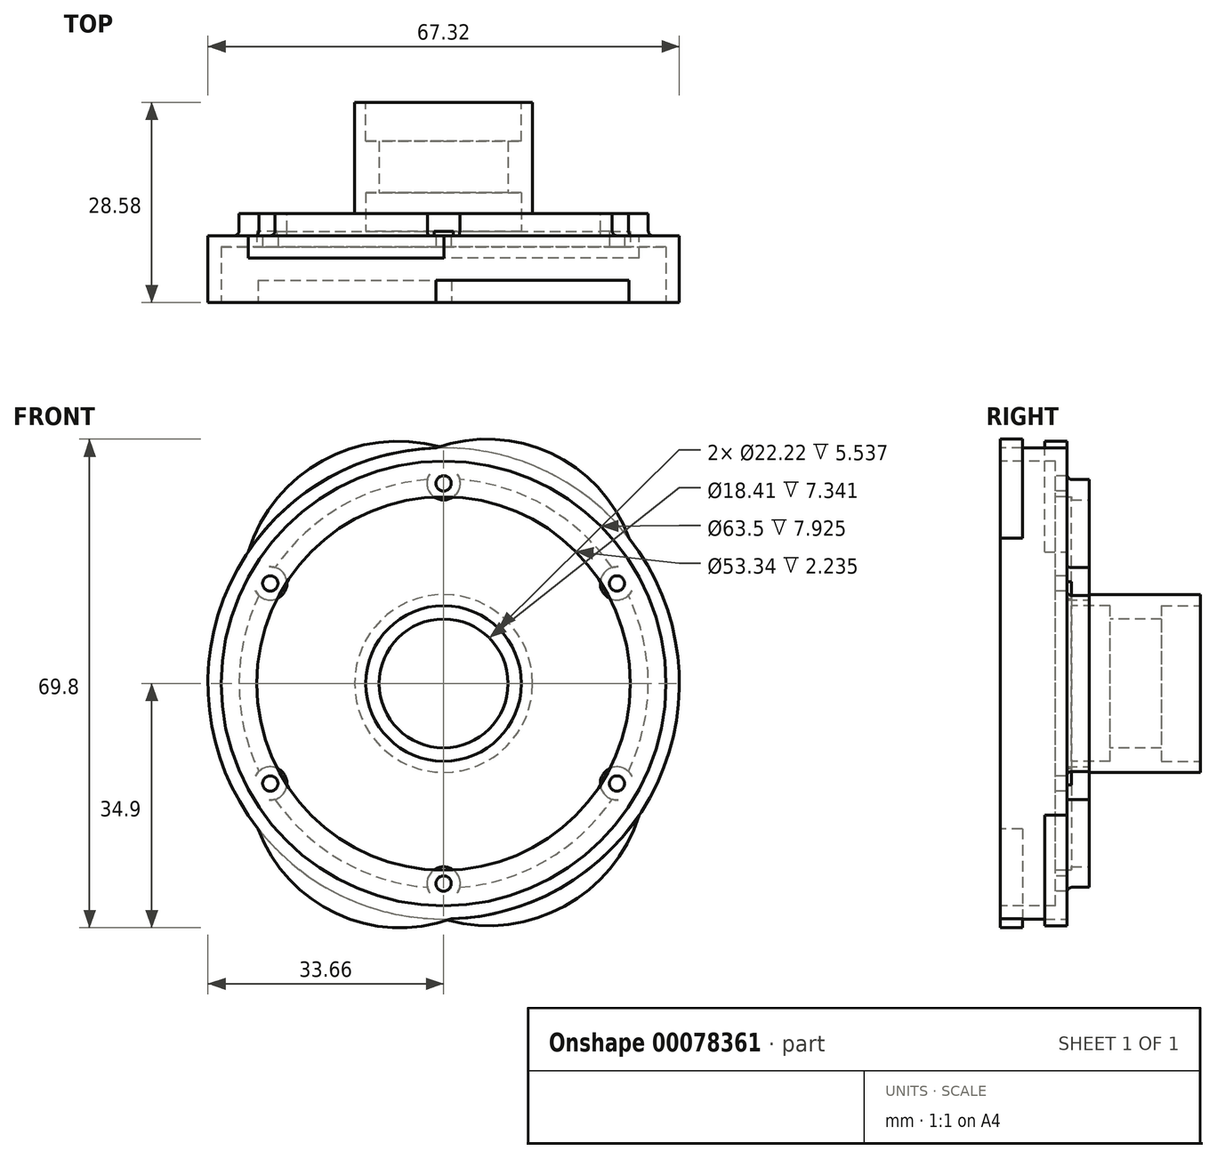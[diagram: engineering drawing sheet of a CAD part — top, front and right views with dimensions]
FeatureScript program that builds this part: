
annotation { "Feature Type Name" : "Feature", "Feature Type Description" : "" }
export const myFeature = defineFeature(function(context is Context, id is Id, definition is map)
    precondition{}
    {
        {
            var Q0;
            Q0=qCreatedBy(makeId("Front.planeOp"),FACE);
            var sketch = newSketch(context, id + "F0", { "sketchPlane" : qUnion([Q0])});
            skCircle(sketch, "E0", {"center": v(0, 0) * mm, "radius": 33.66 * mm});
            skSolve(sketch);
        }
        {
            var Q0;
            Q0 = qSketchRegion(id + "F0", true);
            extrude(context, id + "F1", {"entities" : qUnion([Q0]), "depth" : 28.57 * mm});
        }
        {
            var Q0;
            Q0=makeQuery(id+"F1.opExtrude","CAP_FACE",FACE,{"disambiguationData":[OSD([sQuery(id+"F0.wireOp",EDGE,"E0")])],"isStart":true});
            var sketch = newSketch(context, id + "F2", { "sketchPlane" : qUnion([Q0])});
            skCircle(sketch, "E1", {"center": v(0, 0) * mm, "radius": 12.7 * mm});
            skCircle(sketch, "E2", {"center": v(0, 0) * mm, "radius": 43.85 * mm});
            skSolve(sketch);
        }
        {
            var Q0;
            Q0 = qSketchRegion(id + "F2", true);
            extrude(context, id + "F3", {"entities" : qUnion([Q0]), "operationType" : NewBodyOperationType.REMOVE, "oppositeDirection" : true, "depth" : 15.88 * mm});
        }
        {
            var Q0;
            Q0=makeQuery(id+"F1.opExtrude","CAP_FACE",FACE,{"disambiguationData":[OSD([sQuery(id+"F0.wireOp",EDGE,"E0")])],"isStart":false});
            var sketch = newSketch(context, id + "F4", { "sketchPlane" : qUnion([Q0])});
            skCircle(sketch, "E3", {"center": v(0, 0) * mm, "radius": 31.75 * mm});
            skSolve(sketch);
        }
        {
            var Q0;
            Q0 = qSketchRegion(id + "F4", true);
            extrude(context, id + "F5", {"entities" : qUnion([Q0]), "operationType" : NewBodyOperationType.REMOVE, "oppositeDirection" : true, "depth" : 7.92 * mm});
        }
        {
            var Q0;
            Q0=makeQuery(id+"F5.boolean.opBoolean","COPY",FACE,{"derivedFrom":makeQuery(id+"F5.opExtrude","CAP_FACE",FACE,{"disambiguationData":[OSD([sQuery(id+"F4.wireOp",EDGE,"E3")])],"isStart":false})});
            var sketch = newSketch(context, id + "F6", { "sketchPlane" : qUnion([Q0])});
            skCircle(sketch, "E4", {"center": v(0, 0) * mm, "radius": 26.67 * mm});
            skSolve(sketch);
        }
        {
            var Q0;
            Q0 = qSketchRegion(id + "F6", true);
            extrude(context, id + "F7", {"entities" : qUnion([Q0]), "operationType" : NewBodyOperationType.REMOVE, "oppositeDirection" : true, "depth" : 2.24 * mm});
        }
        {
            var Q0;
            Q0=makeQuery(id+"F7.boolean.opBoolean","COPY",FACE,{"derivedFrom":makeQuery(id+"F7.opExtrude","CAP_FACE",FACE,{"disambiguationData":[OSD([sQuery(id+"F6.wireOp",EDGE,"E4")])],"isStart":false})});
            var sketch = newSketch(context, id + "F8", { "sketchPlane" : qUnion([Q0])});
            skCircle(sketch, "E5", {"center": v(0, 0) * mm, "radius": 11.1 * mm});
            skSolve(sketch);
        }
        {
            var Q0;
            Q0 = qSketchRegion(id + "F8", true);
            extrude(context, id + "F9", {"entities" : qUnion([Q0]), "operationType" : NewBodyOperationType.REMOVE, "oppositeDirection" : true, "depth" : 5.54 * mm});
        }
        {
            var Q0;
            Q0=makeQuery(id+"F9.boolean.opBoolean","COPY",FACE,{"derivedFrom":makeQuery(id+"F9.opExtrude","CAP_FACE",FACE,{"disambiguationData":[OSD([sQuery(id+"F8.wireOp",EDGE,"E5")])],"isStart":false})});
            var sketch = newSketch(context, id + "F10", { "sketchPlane" : qUnion([Q0])});
            skCircle(sketch, "E6", {"center": v(0, 0) * mm, "radius": 9.2 * mm});
            skSolve(sketch);
        }
        {
            var Q0;
            Q0=makeQuery(id+"F10.imprint","IMPRINT",FACE,{"disambiguationData":[TD([[makeQuery(id+"F10.imprint","IMPRINT",EDGE,{"derivedFrom":sQuery(id+"F10.wireOp",EDGE,"E6")}),1.0]])]});
            extrude(context, id + "F11", {"entities" : qUnion([Q0]), "operationType" : NewBodyOperationType.REMOVE, "oppositeDirection" : true, "depth" : 25.4 * mm});
        }
        {
            var Q0;
            Q0=makeQuery(id+"F1.opExtrude","CAP_FACE",FACE,{"disambiguationData":[OSD([sQuery(id+"F0.wireOp",EDGE,"E0")])],"isStart":true});
            var sketch = newSketch(context, id + "F12", { "sketchPlane" : qUnion([Q0])});
            skCircle(sketch, "E7", {"center": v(0, 0) * mm, "radius": 11.1 * mm});
            skSolve(sketch);
        }
        {
            var Q0;
            Q0 = qSketchRegion(id + "F12", true);
            extrude(context, id + "F13", {"entities" : qUnion([Q0]), "operationType" : NewBodyOperationType.REMOVE, "oppositeDirection" : true, "depth" : 5.54 * mm});
        }
        {
            var Q0;
            Q0=makeQuery(id+"F3.boolean.opBoolean","COPY",FACE,{"derivedFrom":makeQuery(id+"F3.opExtrude","CAP_FACE",FACE,{"disambiguationData":[OSD([sQuery(id+"F2.wireOp",EDGE,"E1"),sQuery(id+"F2.wireOp",EDGE,"E2")])],"isStart":false})});
            var sketch = newSketch(context, id + "F14", { "sketchPlane" : qUnion([Q0])});
            skCircle(sketch, "E8", {"center": v(0, 0) * mm, "radius": 29.2 * mm});
            skCircle(sketch, "E9", {"center": v(0, 0) * mm, "radius": 43.76 * mm});
            skSolve(sketch);
        }
        {
            var Q0;
            Q0 = qSketchRegion(id + "F14", true);
            extrude(context, id + "F15", {"entities" : qUnion([Q0]), "operationType" : NewBodyOperationType.REMOVE, "oppositeDirection" : true, "depth" : 3.17 * mm});
        }
        {
            var Q0;
            Q0=makeQuery(id+"F5.boolean.opBoolean","COPY",FACE,{"derivedFrom":makeQuery(id+"F5.opExtrude","CAP_FACE",FACE,{"disambiguationData":[OSD([sQuery(id+"F4.wireOp",EDGE,"E3")])],"isStart":false})});
            var sketch = newSketch(context, id + "F16", { "sketchPlane" : qUnion([Q0])});
            skCircle(sketch, "E10", {"center": v(0, 28.58) * mm, "radius": 1.1 * mm});
            skCircle(sketch, "E11.1.0", {"center": v(-24.75, 14.29) * mm, "radius": 1.1 * mm});
            skCircle(sketch, "E11.2.0", {"center": v(-24.75, -14.29) * mm, "radius": 1.1 * mm});
            skCircle(sketch, "E11.3.0", {"center": v(0, -28.58) * mm, "radius": 1.1 * mm});
            skCircle(sketch, "E11.4.0", {"center": v(24.75, -14.29) * mm, "radius": 1.1 * mm});
            skCircle(sketch, "E11.5.0", {"center": v(24.75, 14.29) * mm, "radius": 1.1 * mm});
            skPoint(sketch, "E11.center", {"position": v(0, 0) * mm});
            skSolve(sketch);
        }
        {
            var Q0;
            Q0 = qSketchRegion(id + "F16", true);
            extrude(context, id + "F17", {"entities" : qUnion([Q0]), "operationType" : NewBodyOperationType.REMOVE, "oppositeDirection" : true, "depth" : 25.4 * mm});
        }
        {
            var Q0;
            Q0=makeQuery(id+"F3.boolean.opBoolean","COPY",FACE,{"derivedFrom":makeQuery(id+"F3.opExtrude","CAP_FACE",FACE,{"disambiguationData":[OSD([sQuery(id+"F2.wireOp",EDGE,"E1"),sQuery(id+"F2.wireOp",EDGE,"E2")])],"isStart":false})});
            var sketch = newSketch(context, id + "F18", { "sketchPlane" : qUnion([Q0])});
            skCircle(sketch, "E12", {"center": v(0, 28.58) * mm, "radius": 2.37 * mm});
            skCircle(sketch, "E13.1.0", {"center": v(-24.75, 14.29) * mm, "radius": 2.37 * mm});
            skCircle(sketch, "E13.2.0", {"center": v(-24.75, -14.29) * mm, "radius": 2.37 * mm});
            skCircle(sketch, "E13.3.0", {"center": v(0, -28.58) * mm, "radius": 2.37 * mm});
            skCircle(sketch, "E13.4.0", {"center": v(24.75, -14.29) * mm, "radius": 2.37 * mm});
            skCircle(sketch, "E13.5.0", {"center": v(24.75, 14.29) * mm, "radius": 2.37 * mm});
            skPoint(sketch, "E13.center", {"position": v(0, 0) * mm});
            skSolve(sketch);
        }
        {
            var Q0;
            Q0 = qSketchRegion(id + "F18", true);
            extrude(context, id + "F19", {"entities" : qUnion([Q0]), "operationType" : NewBodyOperationType.REMOVE, "oppositeDirection" : true, "depth" : 3.17 * mm});
        }
        {
            var Q0;
            {var subQ0=sQuery(id+"F14.wireOp",EDGE,"E8");Q0=makeQuery(id+"F17.boolean.opBoolean","SPLIT",EDGE,{"disambiguationData":[TD([makeQuery(id+"F15.boolean.opBoolean","COPY",FACE,{"derivedFrom":makeQuery(id+"F15.opExtrude","SWEPT_FACE",FACE,{"disambiguationData":[OSD([subQ0])]})}),makeQuery(id+"F15.boolean.opBoolean","COPY",FACE,{"derivedFrom":makeQuery(id+"F15.opExtrude","CAP_FACE",FACE,{"disambiguationData":[OSD([subQ0,sQuery(id+"F14.wireOp",EDGE,"E9")])],"isStart":false})}),makeQuery(id+"F17.opExtrude","SWEPT_FACE",FACE,{"disambiguationData":[OSD([sQuery(id+"F16.wireOp",EDGE,"E10")])]}),makeQuery(id+"F17.opExtrude","SWEPT_FACE",FACE,{"disambiguationData":[OSD([sQuery(id+"F16.wireOp",EDGE,"E11.5.0")])]})])],"derivedFrom":makeQuery(id+"F15.boolean.opBoolean","COPY",EDGE,{"derivedFrom":makeQuery(id+"F15.opExtrude","CAP_EDGE",EDGE,{"disambiguationData":[OSD([subQ0])],"isStart":false})})});}
            var Q1;
            {var subQ0=sQuery(id+"F14.wireOp",EDGE,"E8");Q1=makeQuery(id+"F17.boolean.opBoolean","SPLIT",EDGE,{"disambiguationData":[TD([makeQuery(id+"F15.boolean.opBoolean","COPY",FACE,{"derivedFrom":makeQuery(id+"F15.opExtrude","SWEPT_FACE",FACE,{"disambiguationData":[OSD([subQ0])]})}),makeQuery(id+"F15.boolean.opBoolean","COPY",FACE,{"derivedFrom":makeQuery(id+"F15.opExtrude","CAP_FACE",FACE,{"disambiguationData":[OSD([subQ0,sQuery(id+"F14.wireOp",EDGE,"E9")])],"isStart":false})}),makeQuery(id+"F17.opExtrude","SWEPT_FACE",FACE,{"disambiguationData":[OSD([sQuery(id+"F16.wireOp",EDGE,"E11.4.0")])]}),makeQuery(id+"F17.opExtrude","SWEPT_FACE",FACE,{"disambiguationData":[OSD([sQuery(id+"F16.wireOp",EDGE,"E11.5.0")])]})])],"derivedFrom":makeQuery(id+"F15.boolean.opBoolean","COPY",EDGE,{"derivedFrom":makeQuery(id+"F15.opExtrude","CAP_EDGE",EDGE,{"disambiguationData":[OSD([subQ0])],"isStart":false})})});}
            var Q2;
            {var subQ0=sQuery(id+"F14.wireOp",EDGE,"E8");Q2=makeQuery(id+"F17.boolean.opBoolean","SPLIT",EDGE,{"disambiguationData":[TD([makeQuery(id+"F15.boolean.opBoolean","COPY",FACE,{"derivedFrom":makeQuery(id+"F15.opExtrude","SWEPT_FACE",FACE,{"disambiguationData":[OSD([subQ0])]})}),makeQuery(id+"F15.boolean.opBoolean","COPY",FACE,{"derivedFrom":makeQuery(id+"F15.opExtrude","CAP_FACE",FACE,{"disambiguationData":[OSD([subQ0,sQuery(id+"F14.wireOp",EDGE,"E9")])],"isStart":false})}),makeQuery(id+"F17.opExtrude","SWEPT_FACE",FACE,{"disambiguationData":[OSD([sQuery(id+"F16.wireOp",EDGE,"E11.3.0")])]}),makeQuery(id+"F17.opExtrude","SWEPT_FACE",FACE,{"disambiguationData":[OSD([sQuery(id+"F16.wireOp",EDGE,"E11.4.0")])]})])],"derivedFrom":makeQuery(id+"F15.boolean.opBoolean","COPY",EDGE,{"derivedFrom":makeQuery(id+"F15.opExtrude","CAP_EDGE",EDGE,{"disambiguationData":[OSD([subQ0])],"isStart":false})})});}
            var Q3;
            {var subQ0=sQuery(id+"F14.wireOp",EDGE,"E8");Q3=makeQuery(id+"F17.boolean.opBoolean","SPLIT",EDGE,{"disambiguationData":[TD([makeQuery(id+"F15.boolean.opBoolean","COPY",FACE,{"derivedFrom":makeQuery(id+"F15.opExtrude","SWEPT_FACE",FACE,{"disambiguationData":[OSD([subQ0])]})}),makeQuery(id+"F15.boolean.opBoolean","COPY",FACE,{"derivedFrom":makeQuery(id+"F15.opExtrude","CAP_FACE",FACE,{"disambiguationData":[OSD([subQ0,sQuery(id+"F14.wireOp",EDGE,"E9")])],"isStart":false})}),makeQuery(id+"F17.opExtrude","SWEPT_FACE",FACE,{"disambiguationData":[OSD([sQuery(id+"F16.wireOp",EDGE,"E11.1.0")])]}),makeQuery(id+"F17.opExtrude","SWEPT_FACE",FACE,{"disambiguationData":[OSD([sQuery(id+"F16.wireOp",EDGE,"E11.2.0")])]})])],"derivedFrom":makeQuery(id+"F15.boolean.opBoolean","COPY",EDGE,{"derivedFrom":makeQuery(id+"F15.opExtrude","CAP_EDGE",EDGE,{"disambiguationData":[OSD([subQ0])],"isStart":false})})});}
            var Q4;
            {var subQ0=sQuery(id+"F14.wireOp",EDGE,"E8");Q4=makeQuery(id+"F17.boolean.opBoolean","SPLIT",EDGE,{"disambiguationData":[TD([makeQuery(id+"F15.boolean.opBoolean","COPY",FACE,{"derivedFrom":makeQuery(id+"F15.opExtrude","SWEPT_FACE",FACE,{"disambiguationData":[OSD([subQ0])]})}),makeQuery(id+"F15.boolean.opBoolean","COPY",FACE,{"derivedFrom":makeQuery(id+"F15.opExtrude","CAP_FACE",FACE,{"disambiguationData":[OSD([subQ0,sQuery(id+"F14.wireOp",EDGE,"E9")])],"isStart":false})}),makeQuery(id+"F17.opExtrude","SWEPT_FACE",FACE,{"disambiguationData":[OSD([sQuery(id+"F16.wireOp",EDGE,"E10")])]}),makeQuery(id+"F17.opExtrude","SWEPT_FACE",FACE,{"disambiguationData":[OSD([sQuery(id+"F16.wireOp",EDGE,"E11.1.0")])]})])],"derivedFrom":makeQuery(id+"F15.boolean.opBoolean","COPY",EDGE,{"derivedFrom":makeQuery(id+"F15.opExtrude","CAP_EDGE",EDGE,{"disambiguationData":[OSD([subQ0])],"isStart":false})})});}
            var Q5;
            {var subQ0=sQuery(id+"F14.wireOp",EDGE,"E8");Q5=makeQuery(id+"F17.boolean.opBoolean","SPLIT",EDGE,{"disambiguationData":[TD([makeQuery(id+"F15.boolean.opBoolean","COPY",FACE,{"derivedFrom":makeQuery(id+"F15.opExtrude","SWEPT_FACE",FACE,{"disambiguationData":[OSD([subQ0])]})}),makeQuery(id+"F15.boolean.opBoolean","COPY",FACE,{"derivedFrom":makeQuery(id+"F15.opExtrude","CAP_FACE",FACE,{"disambiguationData":[OSD([subQ0,sQuery(id+"F14.wireOp",EDGE,"E9")])],"isStart":false})}),makeQuery(id+"F17.opExtrude","SWEPT_FACE",FACE,{"disambiguationData":[OSD([sQuery(id+"F16.wireOp",EDGE,"E11.2.0")])]}),makeQuery(id+"F17.opExtrude","SWEPT_FACE",FACE,{"disambiguationData":[OSD([sQuery(id+"F16.wireOp",EDGE,"E11.3.0")])]})])],"derivedFrom":makeQuery(id+"F15.boolean.opBoolean","COPY",EDGE,{"derivedFrom":makeQuery(id+"F15.opExtrude","CAP_EDGE",EDGE,{"disambiguationData":[OSD([subQ0])],"isStart":false})})});}
            var Q6;
            {var subQ0=sQuery(id+"F14.wireOp",EDGE,"E8");Q6=makeQuery(id+"F17.boolean.opBoolean","SPLIT",EDGE,{"disambiguationData":[TD([makeQuery(id+"F3.boolean.opBoolean","COPY",FACE,{"derivedFrom":makeQuery(id+"F3.opExtrude","CAP_FACE",FACE,{"disambiguationData":[OSD([sQuery(id+"F2.wireOp",EDGE,"E1"),sQuery(id+"F2.wireOp",EDGE,"E2")])],"isStart":false})}),makeQuery(id+"F15.boolean.opBoolean","COPY",FACE,{"derivedFrom":makeQuery(id+"F15.opExtrude","SWEPT_FACE",FACE,{"disambiguationData":[OSD([subQ0])]})}),makeQuery(id+"F17.opExtrude","SWEPT_FACE",FACE,{"disambiguationData":[OSD([sQuery(id+"F16.wireOp",EDGE,"E11.2.0")])]}),makeQuery(id+"F17.opExtrude","SWEPT_FACE",FACE,{"disambiguationData":[OSD([sQuery(id+"F16.wireOp",EDGE,"E11.3.0")])]})])],"derivedFrom":makeQuery(id+"F15.boolean.opBoolean","COPY",EDGE,{"derivedFrom":makeQuery(id+"F15.opExtrude","CAP_EDGE",EDGE,{"disambiguationData":[OSD([subQ0])],"isStart":true})})});}
            var Q7;
            {var subQ0=sQuery(id+"F14.wireOp",EDGE,"E8");Q7=makeQuery(id+"F17.boolean.opBoolean","SPLIT",EDGE,{"disambiguationData":[TD([makeQuery(id+"F3.boolean.opBoolean","COPY",FACE,{"derivedFrom":makeQuery(id+"F3.opExtrude","CAP_FACE",FACE,{"disambiguationData":[OSD([sQuery(id+"F2.wireOp",EDGE,"E1"),sQuery(id+"F2.wireOp",EDGE,"E2")])],"isStart":false})}),makeQuery(id+"F15.boolean.opBoolean","COPY",FACE,{"derivedFrom":makeQuery(id+"F15.opExtrude","SWEPT_FACE",FACE,{"disambiguationData":[OSD([subQ0])]})}),makeQuery(id+"F17.opExtrude","SWEPT_FACE",FACE,{"disambiguationData":[OSD([sQuery(id+"F16.wireOp",EDGE,"E11.1.0")])]}),makeQuery(id+"F17.opExtrude","SWEPT_FACE",FACE,{"disambiguationData":[OSD([sQuery(id+"F16.wireOp",EDGE,"E11.2.0")])]})])],"derivedFrom":makeQuery(id+"F15.boolean.opBoolean","COPY",EDGE,{"derivedFrom":makeQuery(id+"F15.opExtrude","CAP_EDGE",EDGE,{"disambiguationData":[OSD([subQ0])],"isStart":true})})});}
            var Q8;
            {var subQ0=sQuery(id+"F14.wireOp",EDGE,"E8");Q8=makeQuery(id+"F17.boolean.opBoolean","SPLIT",EDGE,{"disambiguationData":[TD([makeQuery(id+"F3.boolean.opBoolean","COPY",FACE,{"derivedFrom":makeQuery(id+"F3.opExtrude","CAP_FACE",FACE,{"disambiguationData":[OSD([sQuery(id+"F2.wireOp",EDGE,"E1"),sQuery(id+"F2.wireOp",EDGE,"E2")])],"isStart":false})}),makeQuery(id+"F15.boolean.opBoolean","COPY",FACE,{"derivedFrom":makeQuery(id+"F15.opExtrude","SWEPT_FACE",FACE,{"disambiguationData":[OSD([subQ0])]})}),makeQuery(id+"F17.opExtrude","SWEPT_FACE",FACE,{"disambiguationData":[OSD([sQuery(id+"F16.wireOp",EDGE,"E11.3.0")])]}),makeQuery(id+"F17.opExtrude","SWEPT_FACE",FACE,{"disambiguationData":[OSD([sQuery(id+"F16.wireOp",EDGE,"E11.4.0")])]})])],"derivedFrom":makeQuery(id+"F15.boolean.opBoolean","COPY",EDGE,{"derivedFrom":makeQuery(id+"F15.opExtrude","CAP_EDGE",EDGE,{"disambiguationData":[OSD([subQ0])],"isStart":true})})});}
            var Q9;
            {var subQ0=sQuery(id+"F14.wireOp",EDGE,"E8");Q9=makeQuery(id+"F17.boolean.opBoolean","SPLIT",EDGE,{"disambiguationData":[TD([makeQuery(id+"F3.boolean.opBoolean","COPY",FACE,{"derivedFrom":makeQuery(id+"F3.opExtrude","CAP_FACE",FACE,{"disambiguationData":[OSD([sQuery(id+"F2.wireOp",EDGE,"E1"),sQuery(id+"F2.wireOp",EDGE,"E2")])],"isStart":false})}),makeQuery(id+"F15.boolean.opBoolean","COPY",FACE,{"derivedFrom":makeQuery(id+"F15.opExtrude","SWEPT_FACE",FACE,{"disambiguationData":[OSD([subQ0])]})}),makeQuery(id+"F17.opExtrude","SWEPT_FACE",FACE,{"disambiguationData":[OSD([sQuery(id+"F16.wireOp",EDGE,"E11.4.0")])]}),makeQuery(id+"F17.opExtrude","SWEPT_FACE",FACE,{"disambiguationData":[OSD([sQuery(id+"F16.wireOp",EDGE,"E11.5.0")])]})])],"derivedFrom":makeQuery(id+"F15.boolean.opBoolean","COPY",EDGE,{"derivedFrom":makeQuery(id+"F15.opExtrude","CAP_EDGE",EDGE,{"disambiguationData":[OSD([subQ0])],"isStart":true})})});}
            var Q10;
            {var subQ0=sQuery(id+"F14.wireOp",EDGE,"E8");Q10=makeQuery(id+"F17.boolean.opBoolean","SPLIT",EDGE,{"disambiguationData":[TD([makeQuery(id+"F3.boolean.opBoolean","COPY",FACE,{"derivedFrom":makeQuery(id+"F3.opExtrude","CAP_FACE",FACE,{"disambiguationData":[OSD([sQuery(id+"F2.wireOp",EDGE,"E1"),sQuery(id+"F2.wireOp",EDGE,"E2")])],"isStart":false})}),makeQuery(id+"F15.boolean.opBoolean","COPY",FACE,{"derivedFrom":makeQuery(id+"F15.opExtrude","SWEPT_FACE",FACE,{"disambiguationData":[OSD([subQ0])]})}),makeQuery(id+"F17.opExtrude","SWEPT_FACE",FACE,{"disambiguationData":[OSD([sQuery(id+"F16.wireOp",EDGE,"E10")])]}),makeQuery(id+"F17.opExtrude","SWEPT_FACE",FACE,{"disambiguationData":[OSD([sQuery(id+"F16.wireOp",EDGE,"E11.5.0")])]})])],"derivedFrom":makeQuery(id+"F15.boolean.opBoolean","COPY",EDGE,{"derivedFrom":makeQuery(id+"F15.opExtrude","CAP_EDGE",EDGE,{"disambiguationData":[OSD([subQ0])],"isStart":true})})});}
            var Q11;
            {var subQ0=sQuery(id+"F14.wireOp",EDGE,"E8");Q11=makeQuery(id+"F17.boolean.opBoolean","SPLIT",EDGE,{"disambiguationData":[TD([makeQuery(id+"F3.boolean.opBoolean","COPY",FACE,{"derivedFrom":makeQuery(id+"F3.opExtrude","CAP_FACE",FACE,{"disambiguationData":[OSD([sQuery(id+"F2.wireOp",EDGE,"E1"),sQuery(id+"F2.wireOp",EDGE,"E2")])],"isStart":false})}),makeQuery(id+"F15.boolean.opBoolean","COPY",FACE,{"derivedFrom":makeQuery(id+"F15.opExtrude","SWEPT_FACE",FACE,{"disambiguationData":[OSD([subQ0])]})}),makeQuery(id+"F17.opExtrude","SWEPT_FACE",FACE,{"disambiguationData":[OSD([sQuery(id+"F16.wireOp",EDGE,"E10")])]}),makeQuery(id+"F17.opExtrude","SWEPT_FACE",FACE,{"disambiguationData":[OSD([sQuery(id+"F16.wireOp",EDGE,"E11.1.0")])]})])],"derivedFrom":makeQuery(id+"F15.boolean.opBoolean","COPY",EDGE,{"derivedFrom":makeQuery(id+"F15.opExtrude","CAP_EDGE",EDGE,{"disambiguationData":[OSD([subQ0])],"isStart":true})})});}
            fillet(context, id + "F20", {"entities" : qUnion([Q0, Q1, Q2, Q3, Q4, Q5, Q6, Q7, Q8, Q9, Q10, Q11]), "radius" : 0.76 * mm, "tangentPropagation" : true, "allowEdgeOverflow" : false});
        }
        {
            var Q0;
            Q0=makeQuery(id+"F1.opExtrude","CAP_FACE",FACE,{"disambiguationData":[OSD([sQuery(id+"F0.wireOp",EDGE,"E0")])],"isStart":false});
            var sketch = newSketch(context, id + "F21", { "sketchPlane" : qUnion([Q0])});
            skLineSegment(sketch, "E14", {"start": v(0, 0) * mm, "end": v(17.9, 38.37) * mm, "construction": true});
            skArc(sketch, "E15", {"start": v(27.29, 18.08) * mm, "mid": v(15.33, 32.87) * mm, "end": v(-3.69, 32.53) * mm});
            skArc(sketch, "E16", {"start": v(27.29, 18.08) * mm, "mid": v(13.83, 29.67) * mm, "end": v(-3.69, 32.53) * mm});
            skArc(sketch, "E17.MirrorCS", {"start": v(3.69, -32.53) * mm, "mid": v(-13.83, -29.67) * mm, "end": v(-27.29, -18.08) * mm});
            skArc(sketch, "E18.MirrorCS", {"start": v(3.69, -32.53) * mm, "mid": v(-15.33, -32.87) * mm, "end": v(-27.29, -18.08) * mm});
            skSolve(sketch);
        }
        {
            var Q0;
            Q0 = qSketchRegion(id + "F21", true);
            extrude(context, id + "F22", {"entities" : qUnion([Q0]), "operationType" : NewBodyOperationType.ADD, "oppositeDirection" : true, "depth" : 3.17 * mm});
        }
        {
            var Q0;
            Q0=makeQuery(id+"F19.boolean.opBoolean","MERGE",FACE,{"derivedFrom":[makeQuery(id+"F15.boolean.opBoolean","COPY",FACE,{"derivedFrom":makeQuery(id+"F15.opExtrude","CAP_FACE",FACE,{"disambiguationData":[OSD([sQuery(id+"F14.wireOp",EDGE,"E8"),sQuery(id+"F14.wireOp",EDGE,"E9")])],"isStart":false})}),makeQuery(id+"F19.opExtrude","CAP_FACE",FACE,{"disambiguationData":[OSD([sQuery(id+"F18.wireOp",EDGE,"E12")])],"isStart":false}),makeQuery(id+"F19.opExtrude","CAP_FACE",FACE,{"disambiguationData":[OSD([sQuery(id+"F18.wireOp",EDGE,"E13.1.0")])],"isStart":false}),makeQuery(id+"F19.opExtrude","CAP_FACE",FACE,{"disambiguationData":[OSD([sQuery(id+"F18.wireOp",EDGE,"E13.2.0")])],"isStart":false}),makeQuery(id+"F19.opExtrude","CAP_FACE",FACE,{"disambiguationData":[OSD([sQuery(id+"F18.wireOp",EDGE,"E13.3.0")])],"isStart":false}),makeQuery(id+"F19.opExtrude","CAP_FACE",FACE,{"disambiguationData":[OSD([sQuery(id+"F18.wireOp",EDGE,"E13.4.0")])],"isStart":false}),makeQuery(id+"F19.opExtrude","CAP_FACE",FACE,{"disambiguationData":[OSD([sQuery(id+"F18.wireOp",EDGE,"E13.5.0")])],"isStart":false})]});
            var sketch = newSketch(context, id + "F23", { "sketchPlane" : qUnion([Q0])});
            skLineSegment(sketch, "E19", {"start": v(0, 0) * mm, "end": v(20.67, 38.87) * mm, "construction": true});
            skArc(sketch, "E20", {"start": v(28.64, 15.79) * mm, "mid": v(17, 31.97) * mm, "end": v(-2.93, 32.57) * mm});
            skArc(sketch, "E21", {"start": v(28.64, 15.79) * mm, "mid": v(15.35, 28.87) * mm, "end": v(-2.93, 32.57) * mm});
            skArc(sketch, "E22.MirrorCS", {"start": v(2.93, -32.57) * mm, "mid": v(-15.35, -28.87) * mm, "end": v(-28.64, -15.79) * mm});
            skArc(sketch, "E23.MirrorCS", {"start": v(2.93, -32.57) * mm, "mid": v(-17, -31.97) * mm, "end": v(-28.64, -15.79) * mm});
            skSolve(sketch);
        }
        {
            var Q0;
            Q0 = qSketchRegion(id + "F23", true);
            extrude(context, id + "F24", {"entities" : qUnion([Q0]), "operationType" : NewBodyOperationType.ADD, "oppositeDirection" : true, "depth" : 3.17 * mm});
        }
    });
